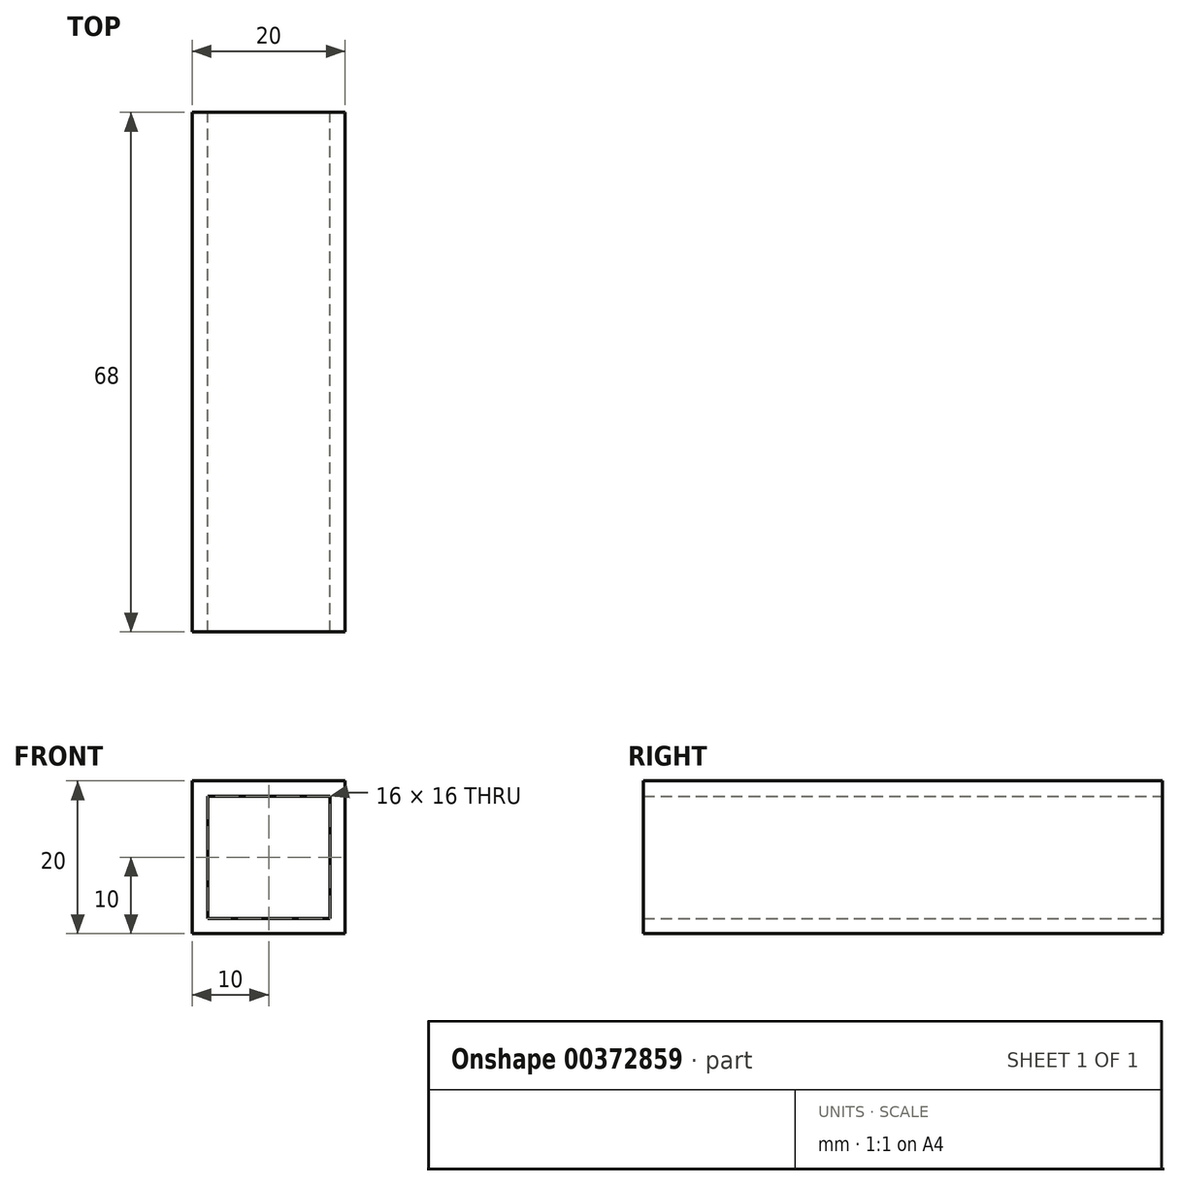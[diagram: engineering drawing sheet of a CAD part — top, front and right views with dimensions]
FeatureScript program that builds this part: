
annotation { "Feature Type Name" : "Feature", "Feature Type Description" : "" }
export const myFeature = defineFeature(function(context is Context, id is Id, definition is map)
    precondition{}
    {
        {
            var Q0;
            Q0=qCreatedBy(makeId("Front.planeOp"),FACE);
            var sketch = newSketch(context, id + "F0", { "sketchPlane" : qUnion([Q0])});
            skLineSegment(sketch, "E0.bottom", {"start": v(0, 0) * mm, "end": v(20, 0) * mm});
            skLineSegment(sketch, "E0.top", {"start": v(0, 20) * mm, "end": v(20, 20) * mm});
            skLineSegment(sketch, "E0.left", {"start": v(0, 0) * mm, "end": v(0, 20) * mm});
            skLineSegment(sketch, "E0.right", {"start": v(20, 0) * mm, "end": v(20, 20) * mm});
            skLineSegment(sketch, "E1.0", {"start": v(2, 18) * mm, "end": v(18, 18) * mm});
            skLineSegment(sketch, "E1.1", {"start": v(2, 2) * mm, "end": v(2, 18) * mm});
            skLineSegment(sketch, "E1.2", {"start": v(2, 2) * mm, "end": v(18, 2) * mm});
            skLineSegment(sketch, "E1.3", {"start": v(18, 2) * mm, "end": v(18, 18) * mm});
            skSolve(sketch);
        }
        {
            var Q0;
            Q0=makeQuery(id+"F0.imprint","IMPRINT",FACE,{"disambiguationData":[TD([[makeQuery(id+"F0.imprint","IMPRINT",EDGE,{"derivedFrom":sQuery(id+"F0.wireOp",EDGE,"E0.bottom")}),1.0]])]});
            extrude(context, id + "F1", {"entities" : qUnion([Q0]), "depth" : 68 * mm});
        }
    });
